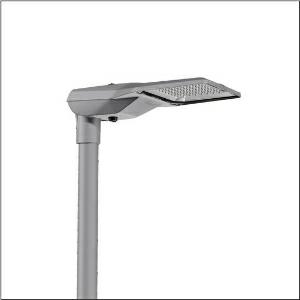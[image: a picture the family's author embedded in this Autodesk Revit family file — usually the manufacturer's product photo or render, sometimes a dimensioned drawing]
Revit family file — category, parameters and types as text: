
# Revit family: streetlight_sl_21_iq_midi___p0_8ab_5xe3r31y08mb_9846
name_source: partatom
category: Lighting Fixtures
units: mm (PartAtom-declared; Revit-internal decimal feet)

## family parameters
Cut with Voids When Loaded = No
Host = Face
Light Source = No
Part Type = Normal
Room Calculation Point = No
Round Connector Dimension = Use Diameter
Shared = No

## types (1)
- --- (1 x LED, 15920 lm, 129.3 W, 3000K)
    Apparent Load = 129 VA
    CIE Flux Codes = 36 71 98 100 100
    Color Rendering = 70
    Color Temperature = 3000K
    Default Elevation = 1800 mm
    Description = Streetlight SL 21 iQ midi, mast luminaire, primary light control with lens, of PMMA, primary optical cover: cover, of toughened safety glass, transparent, light distribution: P0.8aB, light emission: direct distribution, primary light characteristic: asymmetric, installation type: post-top, side-entry, LED, High Power LED, rated luminous flux: 15.920lm, luminous efficacy: 123lm/W, light colour: 730, colour temperature: 3000K, control gear: iQ-Street Remote, D4i with power reduction, control: pre-setting: logarithmic dimming characteristic, Street-Remote, Auto-Match, Temp-Guard, Lumen-Switch, Night-Set, Smart-Wire, Light-Fading, Desk-Remote (wireless, voltage-free reading and setting of iQ features in the workshop via application-optimized NFC function/RFID function), optimised constant luminous flux control (CLO 2.0), mains connection: 230..240V, AC, 50/60Hz, start of lifetime: 129W, end of service life: 142W, reduction: 56W, luminaire housing, of diecast aluminium, powder-coated, SITECO metallic grey (DB 702S), corrosivity category C5 high according to DIN EN ISO 12944, please order mast flange separately, inclination adjustable: 0°, 5°, 10°, 15°, sealing non-destructively replaceable, multi-level sealing system, length: 644mm, width: 335mm, height: 110mm, mast flange for spigot size: 42mm (side-entry): 5XC10008XM4, 60/48mm (side-entry/post-top): 5XC10108XM2, 76/60mm (side-entry/post-top): 5XC10108XM1, mounting height: 4..8m, Smart Interface below and above, protection rating (complete): IP66, insulation class (complete): insulation class II (safety insulation), certification: CE, ENEC, ENEC+, VDE, impact resistance: IK10, permissible operating ambient temperature for outdoor applications: -40..+50°C, standard-compliant lighting for roads and squares, packaging unit: 1 piece

Light Distribution: P0.8aB
    Height = 111 mm
    Lamp = 1 x LED
    Lamp Light Flux = 15920 lm
    Lamp Power = 129.3 W
    Lamp count = 1
    Length = 644 mm
    Luminous efficacy = 123 lm/W
    Manufacturer = Siteco
    ModVariant = No
    Model = 5XE3R31Y08MB
    Number of Poles = 1
    OnlyDefault = Yes
    Power Factor = 1
    Product Name = Streetlight SL 21 iQ midi | P0.8aB
    Product group = mast luminaire | pylon top
    ProductGroupID = 6100
    Protection Class = Protection class II
    Protection Degree = IP 66
    RLX_Detail_Level = 1
    RLX_Emergency_Light_Flux = 0 lm
    RLX_Emergency_Type = 0
    RLX_Emergency_Type_DB = No
    RlxData = <blob elided: 90565 chars, md5=89b791e4>
    Socket = socket
    Standby Power = 0 W
    System Light Flux = 15919 lm
    System Power = 129 W
    Type Comments = factory setting: luminous flux: 100 % | dim-lin: 254 | 672 mA
    Type Image = l_1004304.jpg
    URL = http://relux.com
    VarID = @adj_082937
    Voltage = 0 V
    Weight = 0.00 kg
    Width = 336 mm

## geometry (parser evidence)
native form markers: Blend x4, Sweep x12
no freeform markers — native parametric forms only
